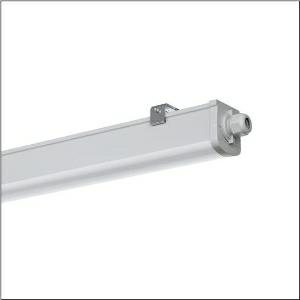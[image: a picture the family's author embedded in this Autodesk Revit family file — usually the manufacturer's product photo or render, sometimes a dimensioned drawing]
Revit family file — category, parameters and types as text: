
# Revit family: monsun_r__31_51fa207k450b_1d2e
name_source: partatom
category: Lighting Fixtures
units: mm (PartAtom-declared; Revit-internal decimal feet)

## family parameters
Cut with Voids When Loaded = No
Host = Face
Light Source = No
Part Type = Normal
Room Calculation Point = No
Round Connector Dimension = Use Diameter
Shared = No

## types (1)
- Monsun® 31 (1 x LED, 5100 lm, 38 W, 4000K)
    Apparent Load = 38 VA
    CIE Flux Codes = 42 72 91 92 100
    Color Rendering = 80
    Color Temperature = 4000K
    Default Elevation = 1800 mm
    Description = Monsun® 31, damp-proof luminaire, primary optical cover: diffuser, of PC, frosted, light emission: direct distribution, primary light characteristic: symmetric, installation type: surface-mounted, LED, rated luminous flux: 5.100lm, luminous efficacy: 134lm/W, light colour: 840, colour temperature: 4000K, control gear: ECG, with terminal, 3+1-pole, max. 2.5mm², through-wiring: 3x 2.5mm² + 1x 1.5mm², mains connection: 220..240V, AC, 50/60Hz, rated input power: 38W, housing, luminaire housing, of PC, light grey (RAL 7035), length: 1.158mm, width: 68mm, height: 76mm, protection rating (complete): IP66, insulation class (complete): insulation class II (safety insulation), certification: CE, ENEC, UKCA, protection symbol: D, impact resistance: IK08, permissible operating ambient temperature: -20..+40°C, corresponds to IFS (International Featured Standards) requirements for safety and quality in the food industry, packaging unit: 1 piece
    Height = 77 mm
    Lamp = 1 x LED
    Lamp Light Flux = 5100 lm
    Lamp Power = 38 W
    Lamp count = 1
    Length = 1218 mm
    Luminous efficacy = 134 lm/W
    Manufacturer = Siteco
    ModVariant = No
    Model = 51FA207K450B
    Mounting Place = Ceiling
    Mounting Type = Surface mounted
    Number of Poles = 1
    OnlyDefault = Yes
    Power Factor = 1
    Product Name = Monsun® 31
    Product group = damp-proof luminaire | ceiling mounted
    ProductGroupID = 300
    Protection Class = Protection class II
    Protection Degree = IP 66
    RLX_Detail_Level = 1
    RlxData = <blob elided: 32769 chars, md5=e6336af6>
    Socket = socket
    Standby Power = 0 W
    System Light Flux = 5100 lm
    System Power = 38 W
    Type Comments = Product without accessories
    Type Image = l_1006174.jpg
    URL = http://relux.com
    VarID = ---
    Voltage = 0 V
    Weight = 0.00 kg
    Width = 69 mm

## geometry (parser evidence)
native form markers: Blend x4, Sweep x14
no freeform markers — native parametric forms only
